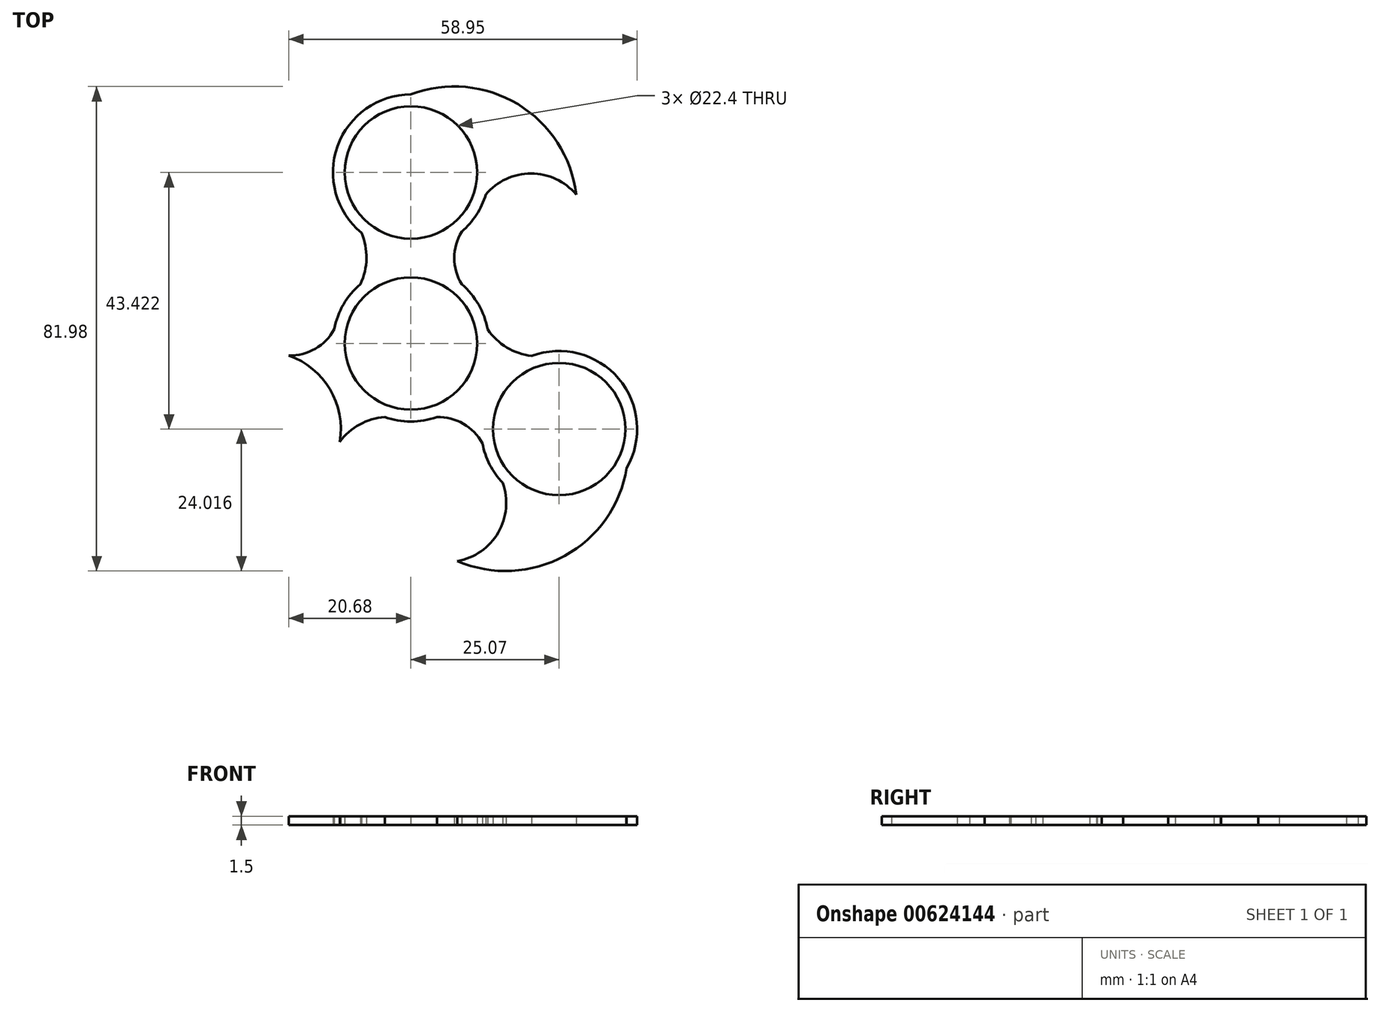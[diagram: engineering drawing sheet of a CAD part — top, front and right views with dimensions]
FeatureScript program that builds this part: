
annotation { "Feature Type Name" : "Feature", "Feature Type Description" : "" }
export const myFeature = defineFeature(function(context is Context, id is Id, definition is map)
    precondition{}
    {
        {
            var Q0;
            Q0=qCreatedBy(makeId("Top.planeOp"),FACE);
            var sketch = newSketch(context, id + "F0", { "sketchPlane" : qUnion([Q0])});
            skCircle(sketch, "E0", {"center": v(0, 0) * mm, "radius": 11.2 * mm});
            skArc(sketch, "E1", {"start": v(-8.56, 10.05) * mm, "mid": v(-11.42, 6.62) * mm, "end": v(-12.97, 2.43) * mm});
            skCircle(sketch, "E2", {"center": v(0, 28.95) * mm, "radius": 11.2 * mm});
            skArc(sketch, "E3", {"start": v(8.59, 18.92) * mm, "mid": v(11.08, 21.78) * mm, "end": v(12.66, 25.22) * mm});
            skCircle(sketch, "E4.1.0", {"center": v(-25.07, -14.47) * mm, "radius": 11.2 * mm});
            skArc(sketch, "E4.1.1", {"start": v(-36.5, -21.07) * mm, "mid": v(-12.94, -19.67) * mm, "end": v(-28.17, -1.64) * mm});
            skCircle(sketch, "E4.2.0", {"center": v(25.07, -14.47) * mm, "radius": 11.2 * mm});
            skArc(sketch, "E4.2.1", {"start": v(12.1, -16.9) * mm, "mid": v(13.32, -20.49) * mm, "end": v(15.51, -23.58) * mm});
            skArc(sketch, "E5", {"start": v(8.59, 18.92) * mm, "mid": v(7.32, 14.47) * mm, "end": v(8.6, 10.02) * mm});
            skArc(sketch, "E6", {"start": v(-8.56, 10.05) * mm, "mid": v(-7.53, 14.38) * mm, "end": v(-8.38, 18.75) * mm});
            skArc(sketch, "E7", {"start": v(27.95, 25.22) * mm, "mid": v(18.1, 40.5) * mm, "end": v(0, 42.15) * mm});
            skArc(sketch, "E8", {"start": v(27.95, 25.22) * mm, "mid": v(20.3, 28.78) * mm, "end": v(12.66, 25.22) * mm});
            skArc(sketch, "E9.1.0", {"start": v(-35.82, 11.6) * mm, "mid": v(-44.12, -4.57) * mm, "end": v(-36.5, -21.07) * mm});
            skArc(sketch, "E9.1.1", {"start": v(-35.82, 11.6) * mm, "mid": v(-35.08, 3.2) * mm, "end": v(-28.17, -1.64) * mm});
            skArc(sketch, "E9.1.2", {"start": v(-20.68, -2.02) * mm, "mid": v(-16.2, -0.9) * mm, "end": v(-12.97, 2.43) * mm});
            skArc(sketch, "E9.1.3", {"start": v(-4.42, -12.44) * mm, "mid": v(-8.69, -13.7) * mm, "end": v(-12.05, -16.63) * mm});
            skArc(sketch, "E9.2.0", {"start": v(7.86, -36.82) * mm, "mid": v(26.02, -35.92) * mm, "end": v(36.5, -21.07) * mm});
            skArc(sketch, "E9.2.1", {"start": v(7.86, -36.82) * mm, "mid": v(14.77, -31.98) * mm, "end": v(15.51, -23.58) * mm});
            skArc(sketch, "E9.2.2", {"start": v(12.1, -16.9) * mm, "mid": v(8.87, -13.57) * mm, "end": v(4.38, -12.45) * mm});
            skArc(sketch, "E9.2.3", {"start": v(12.98, 2.39) * mm, "mid": v(16.22, -0.67) * mm, "end": v(20.42, -2.12) * mm});
            skArc(sketch, "E10.trimOffspring", {"start": v(-4.42, -12.44) * mm, "mid": v(-0.02, -13.2) * mm, "end": v(4.38, -12.45) * mm});
            skArc(sketch, "E11.trimOffspring", {"start": v(12.98, 2.39) * mm, "mid": v(11.44, 6.58) * mm, "end": v(8.6, 10.02) * mm});
            skArc(sketch, "E12.trimOffspring", {"start": v(36.5, -21.07) * mm, "mid": v(35.14, -5.94) * mm, "end": v(20.42, -2.12) * mm});
            skArc(sketch, "E13.trimOffspring", {"start": v(0, 42.15) * mm, "mid": v(-12.43, 33.4) * mm, "end": v(-8.38, 18.75) * mm});
            skSolve(sketch);
        }
        {
            var Q0;
            Q0=makeQuery(id+"F0.imprint","IMPRINT",FACE,{"disambiguationData":[TD([[makeQuery(id+"F0.imprint","IMPRINT",EDGE,{"derivedFrom":sQuery(id+"F0.wireOp",EDGE,"E0")}),-1.0]])]});
            extrude(context, id + "F1", {"entities" : qUnion([Q0]), "depth" : 1.5 * mm, "offsetDistance" : 25 * mm});
        }
    });
